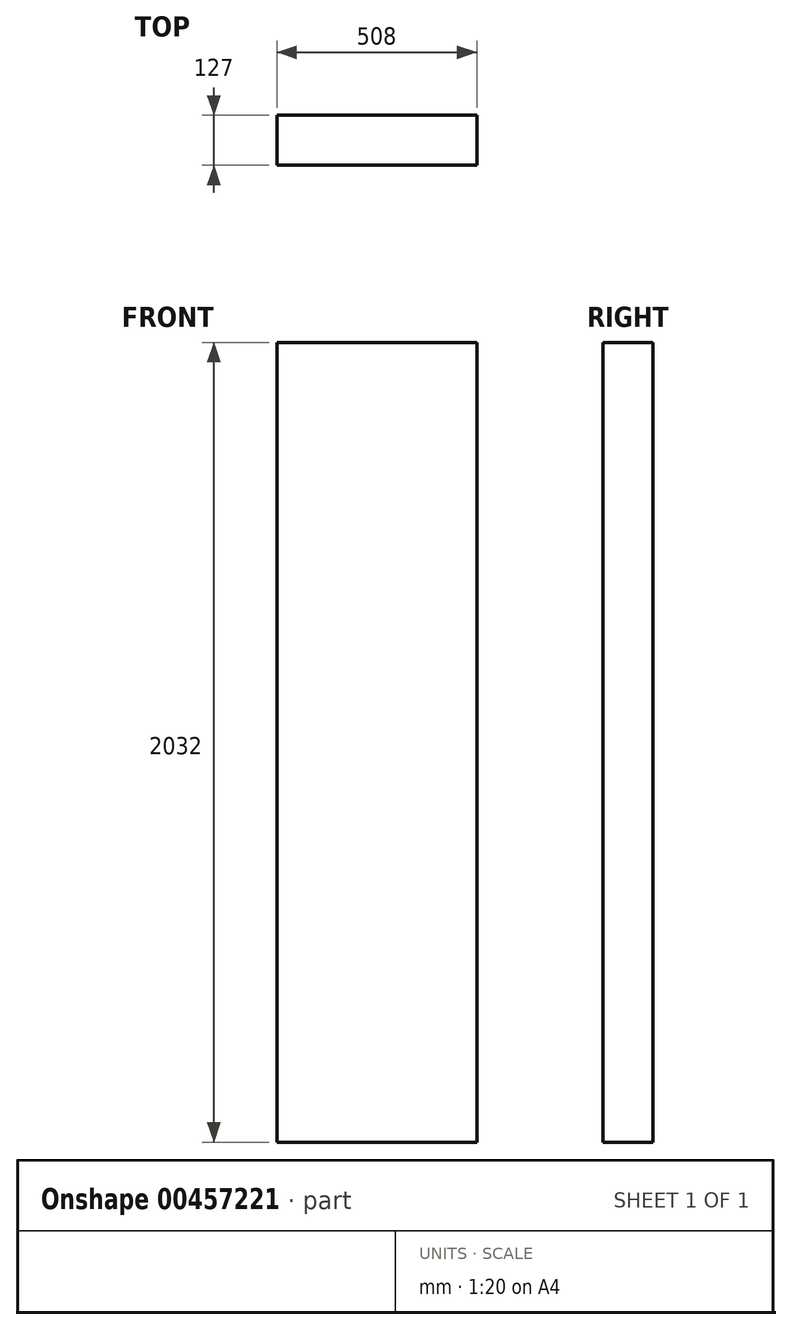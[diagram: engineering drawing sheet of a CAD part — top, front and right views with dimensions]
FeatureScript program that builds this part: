
annotation { "Feature Type Name" : "Feature", "Feature Type Description" : "" }
export const myFeature = defineFeature(function(context is Context, id is Id, definition is map)
    precondition{}
    {
        {
            var Q0;
            Q0=qCreatedBy(makeId("Front.planeOp"),FACE);
            var sketch = newSketch(context, id + "F0", { "sketchPlane" : qUnion([Q0])});
            skLineSegment(sketch, "E0.bottom", {"start": v(-254.18, 1503.94) * mm, "end": v(253.82, 1503.94) * mm});
            skLineSegment(sketch, "E0.top", {"start": v(-254.18, -528.06) * mm, "end": v(253.82, -528.06) * mm});
            skLineSegment(sketch, "E0.left", {"start": v(-254.18, 1503.94) * mm, "end": v(-254.18, -528.06) * mm});
            skLineSegment(sketch, "E0.right", {"start": v(253.82, 1503.94) * mm, "end": v(253.82, -528.06) * mm});
            skSolve(sketch);
        }
        {
            var Q0;
            Q0 = qSketchRegion(id + "F0", true);
            extrude(context, id + "F1", {"entities" : qUnion([Q0]), "depth" : 127 * mm, "symmetric" : true});
        }
    });
